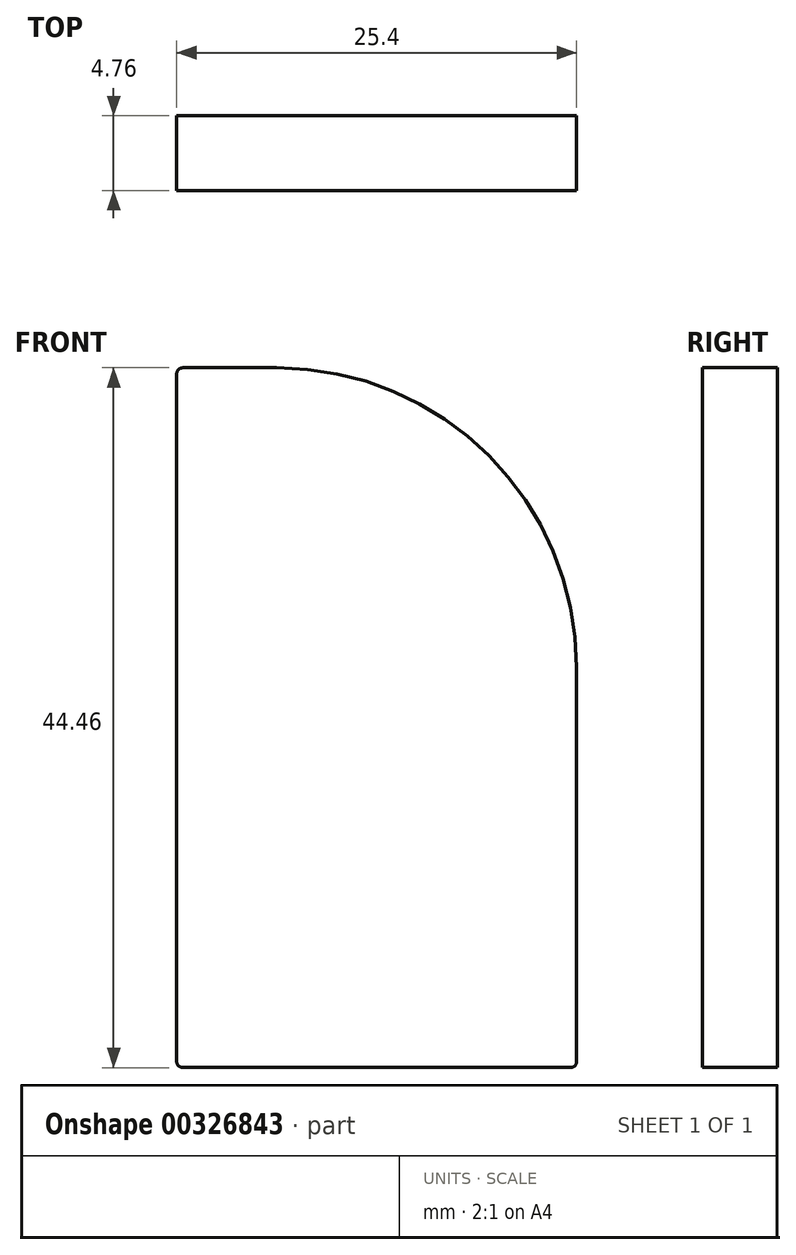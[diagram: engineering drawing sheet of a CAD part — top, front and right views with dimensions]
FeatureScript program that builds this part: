
annotation { "Feature Type Name" : "Feature", "Feature Type Description" : "" }
export const myFeature = defineFeature(function(context is Context, id is Id, definition is map)
    precondition{}
    {
        {
            var Q0;
            Q0=qCreatedBy(makeId("Front.planeOp"),FACE);
            var sketch = newSketch(context, id + "F0", { "sketchPlane" : qUnion([Q0])});
            skLineSegment(sketch, "E0.bottom", {"start": v(-12.7, 22.22) * mm, "end": v(12.7, 22.23) * mm});
            skLineSegment(sketch, "E0.top", {"start": v(-12.7, -22.23) * mm, "end": v(12.7, -22.23) * mm});
            skLineSegment(sketch, "E0.left", {"start": v(-12.7, 22.22) * mm, "end": v(-12.7, -22.23) * mm});
            skLineSegment(sketch, "E0.right", {"start": v(12.7, 22.23) * mm, "end": v(12.7, -22.23) * mm});
            skSolve(sketch);
        }
        {
            var Q0;
            Q0=qSketchRegion(id+"F0",true);
            extrude(context, id + "F1", {"entities" : qUnion([Q0]), "depth" : 4.76 * mm});
        }
        {
            var Q0;
            Q0=makeQuery(id+"F1.opExtrude","SWEPT_EDGE",EDGE,{"disambiguationData":[OSD([sQuery(id+"F0.wireOp",EDGE,"E0.top"),sQuery(id+"F0.wireOp",EDGE,"E0.left")])]});
            var Q1;
            Q1=makeQuery(id+"F1.opExtrude","SWEPT_EDGE",EDGE,{"disambiguationData":[OSD([sQuery(id+"F0.wireOp",EDGE,"E0.top"),sQuery(id+"F0.wireOp",EDGE,"E0.right")])]});
            var Q2;
            Q2=makeQuery(id+"F1.opExtrude","SWEPT_EDGE",EDGE,{"disambiguationData":[OSD([sQuery(id+"F0.wireOp",EDGE,"E0.bottom"),sQuery(id+"F0.wireOp",EDGE,"E0.left")])]});
            fillet(context, id + "F2", {"entities" : qUnion([Q0, Q1, Q2]), "radius" : 0.38 * mm, "tangentPropagation" : true, "allowEdgeOverflow" : false});
        }
        {
            var Q0;
            Q0=makeQuery(id+"F1.opExtrude","SWEPT_EDGE",EDGE,{"disambiguationData":[OSD([sQuery(id+"F0.wireOp",EDGE,"E0.bottom"),sQuery(id+"F0.wireOp",EDGE,"E0.right")])]});
            fillet(context, id + "F3", {"entities" : qUnion([Q0]), "radius" : 19.05 * mm, "tangentPropagation" : true, "allowEdgeOverflow" : false});
        }
    });
